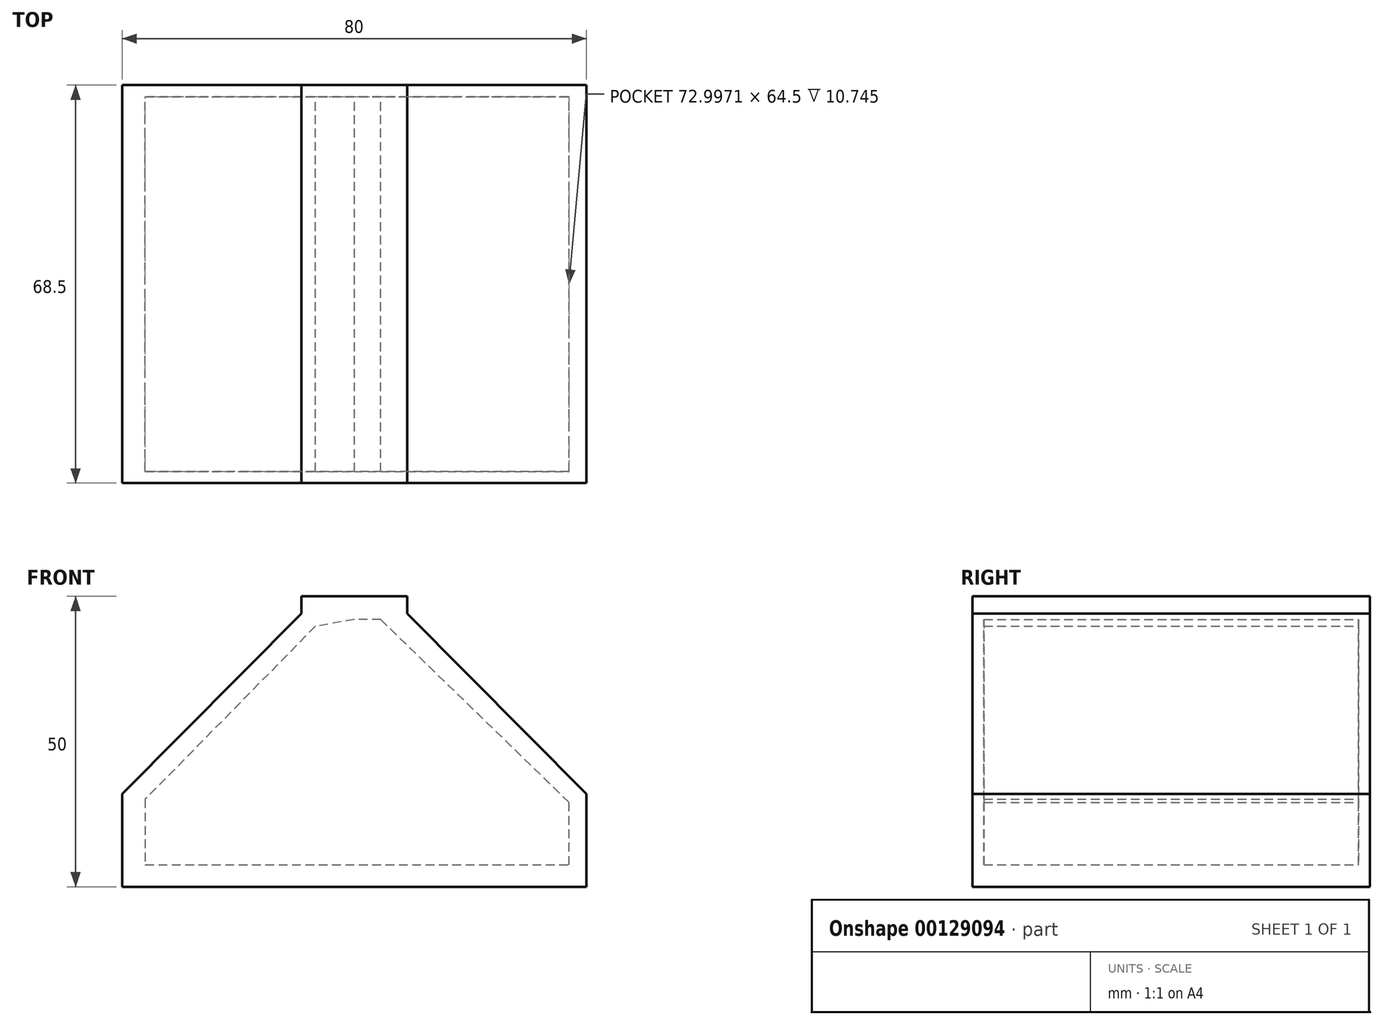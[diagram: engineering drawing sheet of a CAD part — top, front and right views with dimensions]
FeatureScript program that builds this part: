
annotation { "Feature Type Name" : "Feature", "Feature Type Description" : "" }
export const myFeature = defineFeature(function(context is Context, id is Id, definition is map)
    precondition{}
    {
        {
            var Q0;
            Q0=qCreatedBy(makeId("Front.planeOp"),FACE);
            var sketch = newSketch(context, id + "F0", { "sketchPlane" : qUnion([Q0])});
            skLineSegment(sketch, "E0", {"start": v(0, 50) * mm, "end": v(9.14, 50) * mm});
            skLineSegment(sketch, "E1", {"start": v(9.14, 50) * mm, "end": v(9.14, 47) * mm});
            skLineSegment(sketch, "E2", {"start": v(9.14, 47) * mm, "end": v(40, 16) * mm});
            skLineSegment(sketch, "E3", {"start": v(40, 16) * mm, "end": v(40, 0) * mm});
            skLineSegment(sketch, "E4", {"start": v(40, 0) * mm, "end": v(0, 0) * mm});
            skLineSegment(sketch, "E5.MirrorCS", {"start": v(0, 50) * mm, "end": v(-9.14, 50) * mm});
            skLineSegment(sketch, "E6.MirrorCS", {"start": v(-9.14, 47) * mm, "end": v(-40, 16) * mm});
            skLineSegment(sketch, "E7.MirrorCS", {"start": v(-40, 16) * mm, "end": v(-40, 0) * mm});
            skLineSegment(sketch, "E8.MirrorCS", {"start": v(-40, 0) * mm, "end": v(0, 0) * mm});
            skLineSegment(sketch, "E9.MirrorCS", {"start": v(-9.14, 50) * mm, "end": v(-9.14, 47) * mm});
            skLineSegment(sketch, "E10", {"start": v(0, 46) * mm, "end": v(4.57, 46) * mm});
            skPoint(sketch, "E10.endSnap0", {"position": v(4.57, 50) * mm});
            skLineSegment(sketch, "E11", {"start": v(4.57, 46) * mm, "end": v(36.99, 14.51) * mm});
            skLineSegment(sketch, "E12", {"start": v(36.99, 14.51) * mm, "end": v(36.99, 3.77) * mm});
            skLineSegment(sketch, "E13", {"start": v(36.99, 3.77) * mm, "end": v(-36.01, 3.77) * mm});
            skLineSegment(sketch, "E14", {"start": v(-36.01, 3.77) * mm, "end": v(-36.01, 15.06) * mm});
            skLineSegment(sketch, "E15", {"start": v(-36.01, 15.06) * mm, "end": v(-6.7, 44.84) * mm});
            skLineSegment(sketch, "E16", {"start": v(-6.7, 44.84) * mm, "end": v(0, 46) * mm});
            skSolve(sketch);
        }
        {
            var Q0;
            Q0 = qSketchRegion(id + "F0", true);
            extrude(context, id + "F1", {"entities" : qUnion([Q0]), "depth" : 66.5 * mm});
        }
        {
            var Q0;
            Q0=makeQuery(id+"F1.opExtrude","CAP_FACE",FACE,{"disambiguationData":[OSD([sQuery(id+"F0.wireOp",EDGE,"E0"),sQuery(id+"F0.wireOp",EDGE,"E1"),sQuery(id+"F0.wireOp",EDGE,"E2"),sQuery(id+"F0.wireOp",EDGE,"E3"),sQuery(id+"F0.wireOp",EDGE,"E4"),sQuery(id+"F0.wireOp",EDGE,"E5.MirrorCS"),sQuery(id+"F0.wireOp",EDGE,"E6.MirrorCS"),sQuery(id+"F0.wireOp",EDGE,"E7.MirrorCS"),sQuery(id+"F0.wireOp",EDGE,"E8.MirrorCS"),sQuery(id+"F0.wireOp",EDGE,"E9.MirrorCS"),sQuery(id+"F0.wireOp",EDGE,"E10"),sQuery(id+"F0.wireOp",EDGE,"E11"),sQuery(id+"F0.wireOp",EDGE,"E12"),sQuery(id+"F0.wireOp",EDGE,"E13"),sQuery(id+"F0.wireOp",EDGE,"E14"),sQuery(id+"F0.wireOp",EDGE,"E15"),sQuery(id+"F0.wireOp",EDGE,"E16")])],"isStart":false});
            var sketch = newSketch(context, id + "F2", { "sketchPlane" : qUnion([Q0])});
            skLineSegment(sketch, "E17", {"start": v(-9.14, 50) * mm, "end": v(9.14, 50) * mm});
            skLineSegment(sketch, "E18", {"start": v(9.14, 50) * mm, "end": v(9.14, 47) * mm});
            skLineSegment(sketch, "E19", {"start": v(9.14, 47) * mm, "end": v(40, 16) * mm});
            skLineSegment(sketch, "E20", {"start": v(40, 16) * mm, "end": v(40, 0) * mm});
            skLineSegment(sketch, "E21", {"start": v(40, 0) * mm, "end": v(-40, 0) * mm});
            skLineSegment(sketch, "E22", {"start": v(-40, 0) * mm, "end": v(-40, 16) * mm});
            skLineSegment(sketch, "E23", {"start": v(-40, 16) * mm, "end": v(-9.14, 47) * mm});
            skLineSegment(sketch, "E24", {"start": v(-9.14, 47) * mm, "end": v(-9.14, 50) * mm});
            skSolve(sketch);
        }
        {
            var Q0;
            Q0 = qSketchRegion(id + "F2", true);
            extrude(context, id + "F3", {"entities" : qUnion([Q0]), "operationType" : NewBodyOperationType.ADD, "depth" : 2 * mm});
        }
        {
            var Q0;
            Q0=makeQuery(id+"F1.opExtrude","CAP_FACE",FACE,{"disambiguationData":[OSD([sQuery(id+"F0.wireOp",EDGE,"E0"),sQuery(id+"F0.wireOp",EDGE,"E1"),sQuery(id+"F0.wireOp",EDGE,"E2"),sQuery(id+"F0.wireOp",EDGE,"E3"),sQuery(id+"F0.wireOp",EDGE,"E4"),sQuery(id+"F0.wireOp",EDGE,"E5.MirrorCS"),sQuery(id+"F0.wireOp",EDGE,"E6.MirrorCS"),sQuery(id+"F0.wireOp",EDGE,"E7.MirrorCS"),sQuery(id+"F0.wireOp",EDGE,"E8.MirrorCS"),sQuery(id+"F0.wireOp",EDGE,"E9.MirrorCS"),sQuery(id+"F0.wireOp",EDGE,"E10"),sQuery(id+"F0.wireOp",EDGE,"E11"),sQuery(id+"F0.wireOp",EDGE,"E12"),sQuery(id+"F0.wireOp",EDGE,"E13"),sQuery(id+"F0.wireOp",EDGE,"E14"),sQuery(id+"F0.wireOp",EDGE,"E15"),sQuery(id+"F0.wireOp",EDGE,"E16")])],"isStart":true});
            var sketch = newSketch(context, id + "F4", { "sketchPlane" : qUnion([Q0])});
            skLineSegment(sketch, "E25", {"start": v(-9.14, 50) * mm, "end": v(9.14, 50) * mm});
            skLineSegment(sketch, "E26", {"start": v(9.14, 50) * mm, "end": v(9.14, 47) * mm});
            skLineSegment(sketch, "E27", {"start": v(9.14, 47) * mm, "end": v(40, 16) * mm});
            skLineSegment(sketch, "E28", {"start": v(40, 16) * mm, "end": v(40, 0) * mm});
            skLineSegment(sketch, "E29", {"start": v(40, 0) * mm, "end": v(-40, 0) * mm});
            skLineSegment(sketch, "E30", {"start": v(-40, 0) * mm, "end": v(-40, 16) * mm});
            skLineSegment(sketch, "E31", {"start": v(-40, 16) * mm, "end": v(-9.14, 47) * mm});
            skLineSegment(sketch, "E32", {"start": v(-9.14, 47) * mm, "end": v(-9.14, 50) * mm});
            skSolve(sketch);
        }
        {
            var Q0;
            Q0 = qSketchRegion(id + "F4", true);
            extrude(context, id + "F5", {"entities" : qUnion([Q0]), "operationType" : NewBodyOperationType.ADD, "oppositeDirection" : true, "depth" : 2 * mm});
        }
    });
